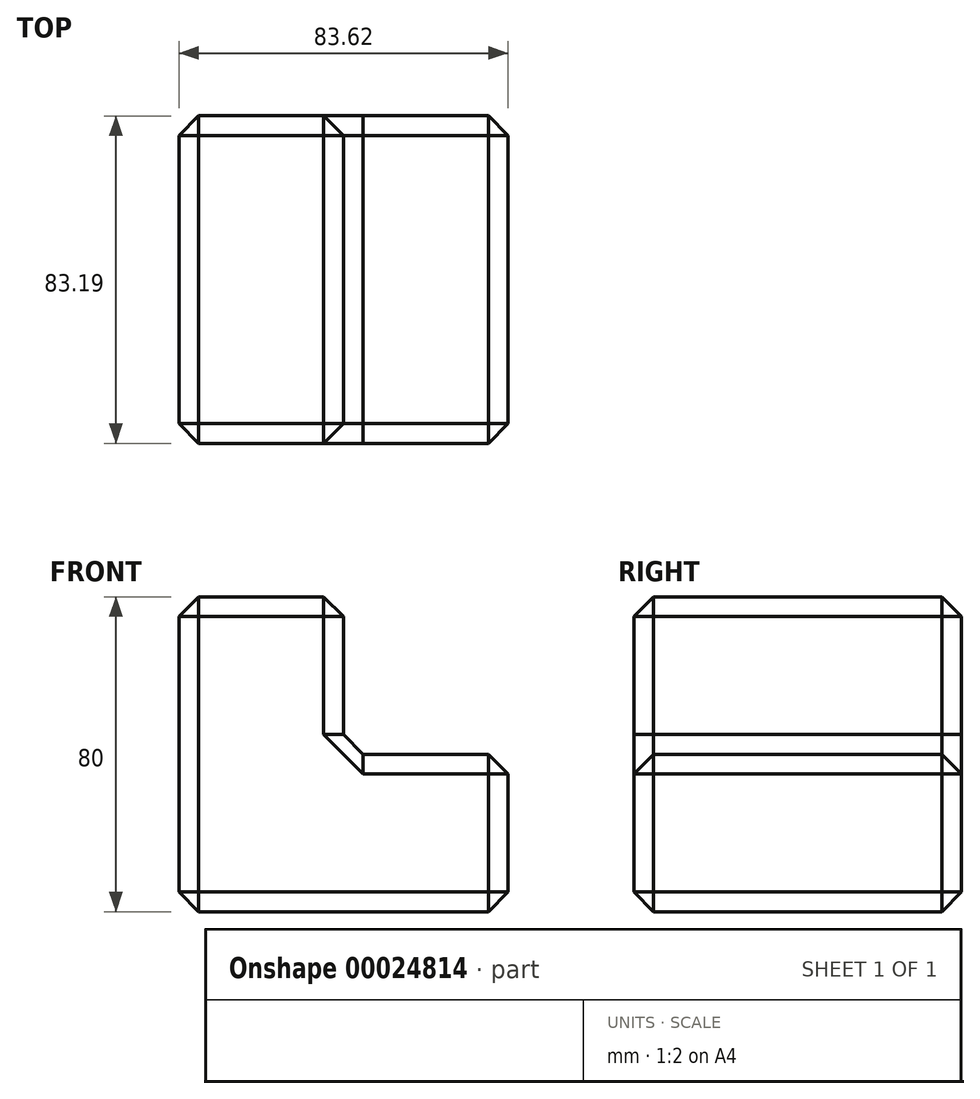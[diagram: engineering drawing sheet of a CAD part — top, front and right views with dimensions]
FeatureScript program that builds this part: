
annotation { "Feature Type Name" : "Feature", "Feature Type Description" : "" }
export const myFeature = defineFeature(function(context is Context, id is Id, definition is map)
    precondition{}
    {
        {
            var Q0;
            Q0=qCreatedBy(makeId("Top.planeOp"),FACE);
            var sketch = newSketch(context, id + "F0", { "sketchPlane" : qUnion([Q0])});
            skLineSegment(sketch, "E0.bottom", {"start": v(-59.13, -45.93) * mm, "end": v(24.5, -45.93) * mm});
            skLineSegment(sketch, "E0.top", {"start": v(-59.13, 37.26) * mm, "end": v(24.5, 37.26) * mm});
            skLineSegment(sketch, "E0.left", {"start": v(-59.13, -45.93) * mm, "end": v(-59.13, 37.26) * mm});
            skLineSegment(sketch, "E0.right", {"start": v(24.5, -45.93) * mm, "end": v(24.5, 37.26) * mm});
            skSolve(sketch);
        }
        {
            var Q0;
            Q0=makeQuery(id+"F0.imprint","IMPRINT",FACE,{"disambiguationData":[TD([[makeQuery(id+"F0.imprint","IMPRINT",EDGE,{"derivedFrom":sQuery(id+"F0.wireOp",EDGE,"E0.bottom")}),1.0]])]});
            extrude(context, id + "F1", {"entities" : qUnion([Q0]), "depth" : 40 * mm});
        }
        {
            var Q0;
            Q0=makeQuery(id+"F1.opExtrude","CAP_FACE",FACE,{"disambiguationData":[OSD([sQuery(id+"F0.wireOp",EDGE,"E0.bottom"),sQuery(id+"F0.wireOp",EDGE,"E0.top"),sQuery(id+"F0.wireOp",EDGE,"E0.left"),sQuery(id+"F0.wireOp",EDGE,"E0.right")])],"isStart":false});
            var sketch = newSketch(context, id + "F2", { "sketchPlane" : qUnion([Q0])});
            skLineSegment(sketch, "E1", {"start": v(-17.32, 37.26) * mm, "end": v(-17.32, -45.93) * mm});
            skSolve(sketch);
        }
        {
            var Q0;
            {var subQ1=sQuery(id+"F2.wireOp",EDGE,"E1");Q0=makeQuery(id+"F2.imprint","IMPRINT",FACE,{"disambiguationData":[TD([[makeQuery(id+"F2.imprint","IMPRINT",EDGE,{"derivedFrom":subQ1}),-1.0]])]});}
            extrude(context, id + "F3", {"entities" : qUnion([Q0]), "operationType" : NewBodyOperationType.ADD, "depth" : 40 * mm});
        }
        {
            var Q0;
            Q0=makeQuery(id+"F3.opExtrude","CAP_FACE",FACE,{"disambiguationData":[OSD([sQuery(id+"F0.wireOp",EDGE,"E0.bottom"),sQuery(id+"F0.wireOp",EDGE,"E0.top"),sQuery(id+"F0.wireOp",EDGE,"E0.left"),sQuery(id+"F2.wireOp",EDGE,"E1")])],"isStart":false});
            var Q1;
            Q1=makeQuery(id+"F3.opExtrude","SWEPT_FACE",FACE,{"disambiguationData":[OSD([sQuery(id+"F2.wireOp",EDGE,"E1")])]});
            var Q2;
            Q2=makeQuery(id+"F1.opExtrude","CAP_FACE",FACE,{"disambiguationData":[OSD([sQuery(id+"F0.wireOp",EDGE,"E0.bottom"),sQuery(id+"F0.wireOp",EDGE,"E0.top"),sQuery(id+"F0.wireOp",EDGE,"E0.left"),sQuery(id+"F0.wireOp",EDGE,"E0.right")])],"isStart":false});
            var Q3;
            Q3=makeQuery(id+"F1.opExtrude","SWEPT_FACE",FACE,{"disambiguationData":[OSD([sQuery(id+"F0.wireOp",EDGE,"E0.right")])]});
            var Q4;
            Q4=makeQuery(id+"F1.opExtrude","CAP_FACE",FACE,{"disambiguationData":[OSD([sQuery(id+"F0.wireOp",EDGE,"E0.bottom"),sQuery(id+"F0.wireOp",EDGE,"E0.top"),sQuery(id+"F0.wireOp",EDGE,"E0.left"),sQuery(id+"F0.wireOp",EDGE,"E0.right")])],"isStart":true});
            var Q5;
            {var subQ0=sQuery(id+"F0.wireOp",EDGE,"E0.top");Q5=makeQuery(id+"F3.boolean.opBoolean","MERGE",FACE,{"derivedFrom":[makeQuery(id+"F1.opExtrude","SWEPT_FACE",FACE,{"disambiguationData":[OSD([subQ0])]}),makeQuery(id+"F3.opExtrude","SWEPT_FACE",FACE,{"disambiguationData":[OSD([subQ0])]})]});}
            var Q6;
            {var subQ0=sQuery(id+"F0.wireOp",EDGE,"E0.bottom");Q6=makeQuery(id+"F3.boolean.opBoolean","MERGE",FACE,{"derivedFrom":[makeQuery(id+"F1.opExtrude","SWEPT_FACE",FACE,{"disambiguationData":[OSD([subQ0])]}),makeQuery(id+"F3.opExtrude","SWEPT_FACE",FACE,{"disambiguationData":[OSD([subQ0])]})]});}
            chamfer(context, id + "F4", {"entities" : qUnion([Q0, Q1, Q2, Q3, Q4, Q5, Q6]), "width" : 5 * mm, "tangentPropagation" : true});
        }
    });
